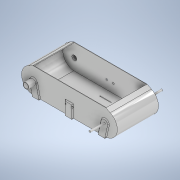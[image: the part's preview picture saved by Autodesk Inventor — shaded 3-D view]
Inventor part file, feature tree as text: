
AUTODESK INVENTOR PART (.ipt)
format: ipt  version: 2021 (Build 250183000, 183)  size: 545,792 bytes
history: native  units: mm
features: extrude x19, sketch x19, projected_geometry x8, fillet x3
ambient origin geometry x8: Origin, YZ Plane, XZ Plane, XY Plane, X Axis, Y Axis, Z Axis, Center Point
bodies: Solid1 (feature_tree)
feature tree (49):
  extrude  "Extrusion1"  Depth=26.0mm
  extrude  "Extrusion3"  Depth=8.0mm
  extrude  "Extrusion4"  Depth=182.8mm TaperAngle=0.0deg
  extrude  "Extrusion5"  Depth=35.0mm TaperAngle=0.0deg
  extrude  "Extrusion6"  Depth=10.0mm TaperAngle=0.0deg
  extrude  "Extrusion7"  Depth=10.0mm
  extrude  "Extrusion8"  Depth=10.0mm
  extrude  "Extrusion12"  Depth=3.0mm
  sketch  "Sketch15"  dims[d42=10.0mm d44=2.0mm]
  extrude  "Extrusion13"  Depth=3.0mm
  sketch  "Sketch17"  dims[d48=4.712389mm d49=3.0mm]
  extrude  "Extrusion14"  Depth=40.0mm
  extrude  "wzmocnienie ramy 1"  Depth=10.0mm
  extrude  "wzmocnienie ramy 2"  Depth=160.0mm
  extrude  "wzmocnienie ramy 3"  TaperAngle=0.0deg  [1 undecoded]
  fillet  "spaw 1"  Radius=10.0mm
  extrude  "wzmocnienie ramy 4"  Depth=4.0mm TaperAngle=0.0deg
  extrude  "wzmocnienie 5"  Depth=4.0mm TaperAngle=0.0deg
  extrude  "wzmocnienie ramy 6"  Depth=4.0mm
  fillet  "spaw 2"  Radius=4.0mm
  extrude  "wzmocnienie ramy 7"  Depth=4.0mm TaperAngle=0.0deg
  extrude  "wzmocnienie ramy 8"  Depth=4.0mm TaperAngle=0.0deg
  extrude  "wzmocnienie ramy 9"  Depth=4.0mm TaperAngle=0.0deg
  fillet  "spaw 3"  Radius=3.9mm
  sketch  "Sketch1"  dims[d0=22.0mm d1=26.0mm]
  sketch  "Sketch3"  dims[d2=35.0mm d3=0.0mm]
  sketch  "Sketch6"  dims[d14=80.0mm d15=45.0mm d16=135.0deg d17=162.5mm d18=135.0deg d19=50.0mm d20=2.0mm d21=0.0mm d22=8.0mm]
  projected_geometry  "Projected Loop1"
  sketch  "Sketch7"  dims[d23=70.0mm d24=0.0mm d26=182.8mm d27=0.0mm]
  projected_geometry  "Projected Loop2"
  projected_geometry  "Projected Loop3"
  sketch  "Sketch8"  dims[d28=2.0mm d29=0.0mm d30=35.0mm d31=0.0mm]
  sketch  "Sketch9"  dims[d32=70.0mm d33=0.0mm d40=10.0mm d41=0.0mm]
  projected_geometry  "Projected Loop5"
  projected_geometry  "Projected Loop6"
  projected_geometry  "Projected Loop7"
  projected_geometry  "Projected Loop8"
  projected_geometry  "Projected Loop9"
  sketch  "Sketch16"  dims[d45=10.0mm d46=0.0mm d47=26.703538mm]
  sketch  "Sketch18"  dims[d50=3.0mm d51=3.0mm]
  sketch  "Sketch19"  dims[d52=50.0mm d53=40.0mm]
  sketch  "Sketch20"  dims[d54=40.0mm d55=20.0mm d57=102.8mm d58=10.0mm d60=10.0mm]
  sketch  "Sketch21"  dims[d62=0.0mm d63=0.0mm d64=160.0mm]
  sketch  "Sketch22"  dims[d65=30.0mm d66=0.0mm d67=10.0mm]
  sketch  "Sketch23"  dims[d68=54.0mm d69=4.0mm d70=0.0mm]
  sketch  "Sketch24"  dims[d71=4.0mm d72=0.0mm d73=4.0mm d74=0.0mm]
  sketch  "Sketch25"  dims[d75=4.0mm d76=30.0mm d77=4.0mm]
  sketch  "Sketch26"  dims[d79=4.0mm d80=4.0mm d81=0.0mm]
  sketch  "Sketch27"  dims[d82=30.0mm d83=4.0mm d84=0.0mm d85=4.0mm d86=0.0mm d87=3.9mm d88=30.0mm d89=4.0mm d90=4.0mm d91=4.0mm d92=0.0mm d93=30.0mm d94=4.0mm d95=0.0mm d96=4.0mm d97=0.0mm d98=3.9mm]
note: 1 required parameter value undecoded (feature->parameter linkage not recoverable at this tier; creation-order binding heuristic only, values carry confidence <= 0.55)
